annotation { "Feature Type Name" : "Feature", "Feature Type Description" : "" }
export const myFeature = defineFeature(function(context is Context, id is Id, definition is map)
    precondition{}
    {
        {
            var Q0;
            Q0=qCreatedBy(makeId("Front.planeOp"),FACE);
            var sketch = newSketch(context, id + "F0", { "sketchPlane" : qUnion([Q0])});
            skLineSegment(sketch, "E0.bottom", {"start": v(-34.13, 36.26) * mm, "end": v(34.87, 36.26) * mm});
            skLineSegment(sketch, "E0.top", {"start": v(-34.13, -16.74) * mm, "end": v(34.87, -16.74) * mm});
            skLineSegment(sketch, "E0.left", {"start": v(-34.13, 36.26) * mm, "end": v(-34.13, -16.74) * mm});
            skLineSegment(sketch, "E0.right", {"start": v(34.87, 36.26) * mm, "end": v(34.87, -16.74) * mm});
            skLineSegment(sketch, "E1", {"start": v(34.87, 23.26) * mm, "end": v(-34.13, 23.26) * mm});
            skLineSegment(sketch, "E2", {"start": v(31.87, 36.26) * mm, "end": v(31.87, 23.26) * mm});
            skLineSegment(sketch, "E3", {"start": v(31.87, 23.26) * mm, "end": v(34.87, 20.26) * mm});
            skLineSegment(sketch, "E4", {"start": v(31.87, -16.74) * mm, "end": v(31.87, 23.26) * mm});
            skLineSegment(sketch, "E5", {"start": v(31.87, -14.74) * mm, "end": v(34.87, -12.7) * mm});
            skLineSegment(sketch, "E6", {"start": v(30.87, 36.26) * mm, "end": v(31.87, 35.26) * mm});
            skCircle(sketch, "E7", {"center": v(-18.63, -14.24) * mm, "radius": 1.5 * mm});
            skCircle(sketch, "E8", {"center": v(-19.13, 33.76) * mm, "radius": 1.5 * mm});
            skCircle(sketch, "E9", {"center": v(32.37, 18.26) * mm, "radius": 1.5 * mm});
            skCircle(sketch, "E10", {"center": v(32.37, -9.74) * mm, "radius": 1.5 * mm});
            skSolve(sketch);
        }
        {
            var Q0;
            {var subQ1=sQuery(id+"F0.wireOp",EDGE,"E0.top");var subQ5=sQuery(id+"F0.wireOp",EDGE,"E0.left");var subQ8=makeQuery(id+"F0.imprint","INTERSECT",VERTEX,{"derivedFrom":[subQ1,subQ5]});Q0=makeQuery(id+"F0.imprint","IMPRINT",FACE,{"disambiguationData":[TD([[makeQuery(id+"F0.imprint","IMPRINT",EDGE,{"disambiguationData":[TD([[subQ8,-1.0]])],"derivedFrom":subQ1}),1.0]])]});}
            var Q1;
            {var subQ0=sQuery(id+"F0.wireOp",EDGE,"E3");Q1=makeQuery(id+"F0.imprint","IMPRINT",FACE,{"disambiguationData":[TD([[makeQuery(id+"F0.imprint","IMPRINT",EDGE,{"derivedFrom":subQ0}),-1.0]])]});}
            var Q2;
            {var subQ3=sQuery(id+"F0.wireOp",EDGE,"E6");Q2=makeQuery(id+"F0.imprint","IMPRINT",FACE,{"disambiguationData":[TD([[makeQuery(id+"F0.imprint","IMPRINT",EDGE,{"derivedFrom":subQ3}),-1.0]])]});}
            extrude(context, id + "F1", {"entities" : qUnion([Q0, Q1, Q2]), "depth" : 1 * mm});
        }
        {
            var Q0;
            Q0=makeQuery(id+"F1.opExtrude","CAP_FACE",FACE,{"disambiguationData":[OSD([sQuery(id+"F0.wireOp",EDGE,"E0.bottom"),sQuery(id+"F0.wireOp",EDGE,"E0.top"),sQuery(id+"F0.wireOp",EDGE,"E0.left"),sQuery(id+"F0.wireOp",EDGE,"E0.right"),sQuery(id+"F0.wireOp",EDGE,"E2"),sQuery(id+"F0.wireOp",EDGE,"E3"),sQuery(id+"F0.wireOp",EDGE,"E4"),sQuery(id+"F0.wireOp",EDGE,"E5"),sQuery(id+"F0.wireOp",EDGE,"E6"),sQuery(id+"F0.wireOp",EDGE,"E7"),sQuery(id+"F0.wireOp",EDGE,"E8"),sQuery(id+"F0.wireOp",EDGE,"E9"),sQuery(id+"F0.wireOp",EDGE,"E10")])],"isStart":false});
            var sketch = newSketch(context, id + "F2", { "sketchPlane" : qUnion([Q0])});
            skLineSegment(sketch, "E11.bottom", {"start": v(30.87, 35.26) * mm, "end": v(9.87, 35.26) * mm});
            skLineSegment(sketch, "E11.top", {"start": v(30.87, 33.26) * mm, "end": v(9.87, 33.26) * mm});
            skLineSegment(sketch, "E11.left", {"start": v(30.87, 35.26) * mm, "end": v(30.87, 33.26) * mm});
            skLineSegment(sketch, "E11.right", {"start": v(9.87, 35.26) * mm, "end": v(9.87, 33.26) * mm});
            skLineSegment(sketch, "E12.bottom", {"start": v(8.87, 35.26) * mm, "end": v(-12.13, 35.26) * mm});
            skLineSegment(sketch, "E12.top", {"start": v(8.87, 33.26) * mm, "end": v(-12.13, 33.26) * mm});
            skLineSegment(sketch, "E12.left", {"start": v(8.87, 35.26) * mm, "end": v(8.87, 33.26) * mm});
            skLineSegment(sketch, "E12.right", {"start": v(-12.13, 35.26) * mm, "end": v(-12.13, 33.26) * mm});
            skLineSegment(sketch, "E13.bottom", {"start": v(30.87, -15.74) * mm, "end": v(15.87, -15.74) * mm});
            skLineSegment(sketch, "E13.top", {"start": v(30.87, -13.74) * mm, "end": v(15.87, -13.74) * mm});
            skLineSegment(sketch, "E13.left", {"start": v(30.87, -15.74) * mm, "end": v(30.87, -13.74) * mm});
            skLineSegment(sketch, "E13.right", {"start": v(15.87, -15.74) * mm, "end": v(15.87, -13.74) * mm});
            skLineSegment(sketch, "E14.bottom", {"start": v(13.87, -15.74) * mm, "end": v(-1.13, -15.74) * mm});
            skLineSegment(sketch, "E14.top", {"start": v(13.87, -13.74) * mm, "end": v(-1.13, -13.74) * mm});
            skLineSegment(sketch, "E14.left", {"start": v(13.87, -15.74) * mm, "end": v(13.87, -13.74) * mm});
            skLineSegment(sketch, "E14.right", {"start": v(-1.13, -15.74) * mm, "end": v(-1.13, -13.74) * mm});
            skLineSegment(sketch, "E15.bottom", {"start": v(-19.65, 29.26) * mm, "end": v(-9.65, 29.26) * mm});
            skLineSegment(sketch, "E15.top", {"start": v(-19.65, 22.06) * mm, "end": v(-9.65, 22.06) * mm});
            skLineSegment(sketch, "E15.left", {"start": v(-19.65, 29.26) * mm, "end": v(-19.65, 22.06) * mm});
            skLineSegment(sketch, "E15.right", {"start": v(-9.65, 29.26) * mm, "end": v(-9.65, 22.06) * mm});
            skSolve(sketch);
        }
        {
            var Q0;
            Q0=makeQuery(id+"F1.opExtrude","CAP_FACE",FACE,{"disambiguationData":[OSD([sQuery(id+"F0.wireOp",EDGE,"E0.bottom"),sQuery(id+"F0.wireOp",EDGE,"E0.top"),sQuery(id+"F0.wireOp",EDGE,"E0.left"),sQuery(id+"F0.wireOp",EDGE,"E0.right"),sQuery(id+"F0.wireOp",EDGE,"E2"),sQuery(id+"F0.wireOp",EDGE,"E3"),sQuery(id+"F0.wireOp",EDGE,"E4"),sQuery(id+"F0.wireOp",EDGE,"E5"),sQuery(id+"F0.wireOp",EDGE,"E6"),sQuery(id+"F0.wireOp",EDGE,"E7"),sQuery(id+"F0.wireOp",EDGE,"E8"),sQuery(id+"F0.wireOp",EDGE,"E9"),sQuery(id+"F0.wireOp",EDGE,"E10")])],"isStart":false});
            var sketch = newSketch(context, id + "F3", { "sketchPlane" : qUnion([Q0])});
            skLineSegment(sketch, "E16.bottom", {"start": v(30.87, -5.74) * mm, "end": v(-5.13, -5.74) * mm});
            skLineSegment(sketch, "E16.top", {"start": v(30.87, 3.26) * mm, "end": v(-5.13, 3.26) * mm});
            skLineSegment(sketch, "E16.left", {"start": v(30.87, -5.74) * mm, "end": v(30.87, 3.26) * mm});
            skLineSegment(sketch, "E16.right", {"start": v(-5.13, -5.74) * mm, "end": v(-5.13, 3.26) * mm});
            skSolve(sketch);
        }
        {
            var Q0;
            Q0=qSketchRegion(id+"F3",true);
            extrude(context, id + "F4", {"entities" : qUnion([Q0]), "depth" : 8 * mm});
        }
        {
            var Q0;
            Q0=makeQuery(id+"F1.opExtrude","CAP_FACE",FACE,{"disambiguationData":[OSD([sQuery(id+"F0.wireOp",EDGE,"E0.bottom"),sQuery(id+"F0.wireOp",EDGE,"E0.top"),sQuery(id+"F0.wireOp",EDGE,"E0.left"),sQuery(id+"F0.wireOp",EDGE,"E0.right"),sQuery(id+"F0.wireOp",EDGE,"E2"),sQuery(id+"F0.wireOp",EDGE,"E3"),sQuery(id+"F0.wireOp",EDGE,"E4"),sQuery(id+"F0.wireOp",EDGE,"E5"),sQuery(id+"F0.wireOp",EDGE,"E6"),sQuery(id+"F0.wireOp",EDGE,"E7"),sQuery(id+"F0.wireOp",EDGE,"E8"),sQuery(id+"F0.wireOp",EDGE,"E9"),sQuery(id+"F0.wireOp",EDGE,"E10")])],"isStart":false});
            var sketch = newSketch(context, id + "F5", { "sketchPlane" : qUnion([Q0])});
            skLineSegment(sketch, "E17.bottom", {"start": v(23.87, 6.26) * mm, "end": v(18.87, 6.26) * mm});
            skLineSegment(sketch, "E17.top", {"start": v(23.87, 11.26) * mm, "end": v(18.87, 11.26) * mm});
            skLineSegment(sketch, "E17.left", {"start": v(23.87, 6.26) * mm, "end": v(23.87, 11.26) * mm});
            skLineSegment(sketch, "E17.right", {"start": v(18.87, 6.26) * mm, "end": v(18.87, 11.26) * mm});
            skCircle(sketch, "E18", {"center": v(21.37, 8.76) * mm, "radius": 1.5 * mm});
            skPoint(sketch, "E18.centerSnap0", {"position": v(23.87, 8.76) * mm});
            skSolve(sketch);
        }
        {
            var Q0;
            Q0=qSketchRegion(id+"F5",true);
            extrude(context, id + "F6", {"entities" : qUnion([Q0]), "depth" : 4 * mm});
        }
        {
            var Q0;
            Q0=makeQuery(id+"F1.opExtrude","CAP_FACE",FACE,{"disambiguationData":[OSD([sQuery(id+"F0.wireOp",EDGE,"E0.bottom"),sQuery(id+"F0.wireOp",EDGE,"E0.top"),sQuery(id+"F0.wireOp",EDGE,"E0.left"),sQuery(id+"F0.wireOp",EDGE,"E0.right"),sQuery(id+"F0.wireOp",EDGE,"E2"),sQuery(id+"F0.wireOp",EDGE,"E3"),sQuery(id+"F0.wireOp",EDGE,"E4"),sQuery(id+"F0.wireOp",EDGE,"E5"),sQuery(id+"F0.wireOp",EDGE,"E6"),sQuery(id+"F0.wireOp",EDGE,"E7"),sQuery(id+"F0.wireOp",EDGE,"E8"),sQuery(id+"F0.wireOp",EDGE,"E9"),sQuery(id+"F0.wireOp",EDGE,"E10")])],"isStart":false});
            var sketch = newSketch(context, id + "F7", { "sketchPlane" : qUnion([Q0])});
            skLineSegment(sketch, "E19.bottom", {"start": v(-23.13, -13.74) * mm, "end": v(-37.13, -13.74) * mm});
            skLineSegment(sketch, "E19.top", {"start": v(-23.13, -5.74) * mm, "end": v(-37.13, -5.74) * mm});
            skLineSegment(sketch, "E19.left", {"start": v(-23.13, -13.74) * mm, "end": v(-23.13, -5.74) * mm});
            skLineSegment(sketch, "E19.right", {"start": v(-37.13, -13.74) * mm, "end": v(-37.13, -5.74) * mm});
            skSolve(sketch);
        }
        {
            var Q0;
            Q0=qSketchRegion(id+"F7",true);
            extrude(context, id + "F8", {"entities" : qUnion([Q0]), "depth" : 10 * mm});
        }
        {
            var Q0;
            Q0=makeQuery(id+"F1.opExtrude","CAP_FACE",FACE,{"disambiguationData":[OSD([sQuery(id+"F0.wireOp",EDGE,"E0.bottom"),sQuery(id+"F0.wireOp",EDGE,"E0.top"),sQuery(id+"F0.wireOp",EDGE,"E0.left"),sQuery(id+"F0.wireOp",EDGE,"E0.right"),sQuery(id+"F0.wireOp",EDGE,"E2"),sQuery(id+"F0.wireOp",EDGE,"E3"),sQuery(id+"F0.wireOp",EDGE,"E4"),sQuery(id+"F0.wireOp",EDGE,"E5"),sQuery(id+"F0.wireOp",EDGE,"E6"),sQuery(id+"F0.wireOp",EDGE,"E7"),sQuery(id+"F0.wireOp",EDGE,"E8"),sQuery(id+"F0.wireOp",EDGE,"E9"),sQuery(id+"F0.wireOp",EDGE,"E10")])],"isStart":false});
            var sketch = newSketch(context, id + "F9", { "sketchPlane" : qUnion([Q0])});
            skLineSegment(sketch, "E20.bottom", {"start": v(-28.13, 21.26) * mm, "end": v(-36.13, 21.26) * mm});
            skLineSegment(sketch, "E20.top", {"start": v(-28.13, 28.26) * mm, "end": v(-36.13, 28.26) * mm});
            skLineSegment(sketch, "E20.left", {"start": v(-28.13, 21.26) * mm, "end": v(-28.13, 28.26) * mm});
            skLineSegment(sketch, "E20.right", {"start": v(-36.13, 21.26) * mm, "end": v(-36.13, 28.26) * mm});
            skSolve(sketch);
        }
        {
            var Q0;
            Q0=qSketchRegion(id+"F9",true);
            extrude(context, id + "F10", {"entities" : qUnion([Q0]), "depth" : 4 * mm});
        }
        {
            var Q0;
            Q0=makeQuery(id+"F1.opExtrude","CAP_FACE",FACE,{"disambiguationData":[OSD([sQuery(id+"F0.wireOp",EDGE,"E0.bottom"),sQuery(id+"F0.wireOp",EDGE,"E0.top"),sQuery(id+"F0.wireOp",EDGE,"E0.left"),sQuery(id+"F0.wireOp",EDGE,"E0.right"),sQuery(id+"F0.wireOp",EDGE,"E2"),sQuery(id+"F0.wireOp",EDGE,"E3"),sQuery(id+"F0.wireOp",EDGE,"E4"),sQuery(id+"F0.wireOp",EDGE,"E5"),sQuery(id+"F0.wireOp",EDGE,"E6"),sQuery(id+"F0.wireOp",EDGE,"E7"),sQuery(id+"F0.wireOp",EDGE,"E8"),sQuery(id+"F0.wireOp",EDGE,"E9"),sQuery(id+"F0.wireOp",EDGE,"E10")])],"isStart":false});
            var sketch = newSketch(context, id + "F11", { "sketchPlane" : qUnion([Q0])});
            skLineSegment(sketch, "E21.bottom", {"start": v(-34.13, 16.26) * mm, "end": v(-30.13, 16.26) * mm});
            skLineSegment(sketch, "E21.top", {"start": v(-34.13, 5.26) * mm, "end": v(-30.13, 5.26) * mm});
            skLineSegment(sketch, "E21.left", {"start": v(-34.13, 16.26) * mm, "end": v(-34.13, 5.26) * mm});
            skLineSegment(sketch, "E21.right", {"start": v(-30.13, 16.26) * mm, "end": v(-30.13, 5.26) * mm});
            skSolve(sketch);
        }
        {
            var Q0;
            Q0=qSketchRegion(id+"F11",true);
            extrude(context, id + "F12", {"entities" : qUnion([Q0]), "depth" : 5 * mm});
        }
        {
            var Q0;
            Q0=makeQuery(id+"F1.opExtrude","CAP_FACE",FACE,{"disambiguationData":[OSD([sQuery(id+"F0.wireOp",EDGE,"E0.bottom"),sQuery(id+"F0.wireOp",EDGE,"E0.top"),sQuery(id+"F0.wireOp",EDGE,"E0.left"),sQuery(id+"F0.wireOp",EDGE,"E0.right"),sQuery(id+"F0.wireOp",EDGE,"E2"),sQuery(id+"F0.wireOp",EDGE,"E3"),sQuery(id+"F0.wireOp",EDGE,"E4"),sQuery(id+"F0.wireOp",EDGE,"E5"),sQuery(id+"F0.wireOp",EDGE,"E6"),sQuery(id+"F0.wireOp",EDGE,"E7"),sQuery(id+"F0.wireOp",EDGE,"E8"),sQuery(id+"F0.wireOp",EDGE,"E9"),sQuery(id+"F0.wireOp",EDGE,"E10")])],"isStart":true});
            var sketch = newSketch(context, id + "F13", { "sketchPlane" : qUnion([Q0])});
            skText(sketch, "E22", { "text": "Olivia Xia\nDebbie Dong", "fontName": "AllertaStencil-Regular.ttf"});
            const initialGuessF13  = {"E22": [-0.00697, 0.0177, 1, 0, 0.00325]};
            skSetInitialGuess(sketch, initialGuessF13);
            skSolve(sketch);
        }
        {
            var Q0;
            Q0=qSketchRegion(id+"F13",true);
            extrude(context, id + "F14", {"entities" : qUnion([Q0]), "operationType" : NewBodyOperationType.ADD, "depth" : .1 * mm});
        }
        {
            var Q0;
            Q0=makeQuery(id+"F5.imprint","IMPRINT",FACE,{"disambiguationData":[TD([[makeQuery(id+"F5.imprint","IMPRINT",EDGE,{"derivedFrom":sQuery(id+"F5.wireOp",EDGE,"E18")}),1.0]])]});
            extrude(context, id + "F15", {"entities" : qUnion([Q0]), "depth" : 5 * mm});
        }
        {
            var Q0;
            Q0=makeQuery(id+"F2.imprint","IMPRINT",FACE,{"disambiguationData":[TD([[makeQuery(id+"F2.imprint","IMPRINT",EDGE,{"derivedFrom":sQuery(id+"F2.wireOp",EDGE,"E15.bottom")}),-1.0]])]});
            extrude(context, id + "F16", {"entities" : qUnion([Q0]), "depth" : 1 * mm});
        }
        {
            var Q0;
            Q0=makeQuery(id+"F2.imprint","IMPRINT",FACE,{"disambiguationData":[TD([[makeQuery(id+"F2.imprint","IMPRINT",EDGE,{"derivedFrom":sQuery(id+"F2.wireOp",EDGE,"E12.bottom")}),1.0]])]});
            var Q1;
            Q1=makeQuery(id+"F2.imprint","IMPRINT",FACE,{"disambiguationData":[TD([[makeQuery(id+"F2.imprint","IMPRINT",EDGE,{"derivedFrom":sQuery(id+"F2.wireOp",EDGE,"E11.bottom")}),1.0]])]});
            var Q2;
            Q2=makeQuery(id+"F2.imprint","IMPRINT",FACE,{"disambiguationData":[TD([[makeQuery(id+"F2.imprint","IMPRINT",EDGE,{"derivedFrom":sQuery(id+"F2.wireOp",EDGE,"E14.bottom")}),-1.0]])]});
            var Q3;
            Q3=makeQuery(id+"F2.imprint","IMPRINT",FACE,{"disambiguationData":[TD([[makeQuery(id+"F2.imprint","IMPRINT",EDGE,{"derivedFrom":sQuery(id+"F2.wireOp",EDGE,"E13.bottom")}),-1.0]])]});
            extrude(context, id + "F17", {"entities" : qUnion([Q0, Q1, Q2, Q3]), "depth" : 8 * mm});
        }
        {
            var Q0;
            Q0=makeQuery(id+"F1.opExtrude","CAP_FACE",FACE,{"disambiguationData":[OSD([sQuery(id+"F0.wireOp",EDGE,"E0.bottom"),sQuery(id+"F0.wireOp",EDGE,"E0.top"),sQuery(id+"F0.wireOp",EDGE,"E0.left"),sQuery(id+"F0.wireOp",EDGE,"E0.right"),sQuery(id+"F0.wireOp",EDGE,"E2"),sQuery(id+"F0.wireOp",EDGE,"E3"),sQuery(id+"F0.wireOp",EDGE,"E4"),sQuery(id+"F0.wireOp",EDGE,"E5"),sQuery(id+"F0.wireOp",EDGE,"E6"),sQuery(id+"F0.wireOp",EDGE,"E7"),sQuery(id+"F0.wireOp",EDGE,"E8"),sQuery(id+"F0.wireOp",EDGE,"E9"),sQuery(id+"F0.wireOp",EDGE,"E10")])],"isStart":false});
            var sketch = newSketch(context, id + "F18", { "sketchPlane" : qUnion([Q0])});
            skLineSegment(sketch, "E23.bottom", {"start": v(-31.63, 2.76) * mm, "end": v(-27.23, 2.76) * mm});
            skLineSegment(sketch, "E23.top", {"start": v(-31.63, -3.24) * mm, "end": v(-27.23, -3.24) * mm});
            skLineSegment(sketch, "E23.left", {"start": v(-31.63, 2.76) * mm, "end": v(-31.63, -3.24) * mm});
            skLineSegment(sketch, "E23.right", {"start": v(-27.23, 2.76) * mm, "end": v(-27.23, -3.24) * mm});
            skLineSegment(sketch, "E24.bottom", {"start": v(-28.61, 13.3) * mm, "end": v(-26.61, 13.3) * mm});
            skLineSegment(sketch, "E24.top", {"start": v(-28.61, 8.3) * mm, "end": v(-26.61, 8.3) * mm});
            skLineSegment(sketch, "E24.left", {"start": v(-28.61, 13.3) * mm, "end": v(-28.61, 8.3) * mm});
            skLineSegment(sketch, "E24.right", {"start": v(-26.61, 13.3) * mm, "end": v(-26.61, 8.3) * mm});
            skSolve(sketch);
        }
        {
            var Q0;
            Q0=makeQuery(id+"F18.imprint","IMPRINT",FACE,{"disambiguationData":[TD([[makeQuery(id+"F18.imprint","IMPRINT",EDGE,{"derivedFrom":sQuery(id+"F18.wireOp",EDGE,"E23.bottom")}),-1.0]])]});
            extrude(context, id + "F19", {"entities" : qUnion([Q0]), "depth" : 2 * mm});
        }
        {
            var Q0;
            Q0=makeQuery(id+"F18.imprint","IMPRINT",FACE,{"disambiguationData":[TD([[makeQuery(id+"F18.imprint","IMPRINT",EDGE,{"derivedFrom":sQuery(id+"F18.wireOp",EDGE,"E24.bottom")}),-1.0]])]});
            extrude(context, id + "F20", {"entities" : qUnion([Q0]), "depth" : 11 * mm});
        }
        {
            var Q0;
            Q0=makeQuery(id+"F1.opExtrude","CAP_FACE",FACE,{"disambiguationData":[OSD([sQuery(id+"F0.wireOp",EDGE,"E0.bottom"),sQuery(id+"F0.wireOp",EDGE,"E0.top"),sQuery(id+"F0.wireOp",EDGE,"E0.left"),sQuery(id+"F0.wireOp",EDGE,"E0.right"),sQuery(id+"F0.wireOp",EDGE,"E2"),sQuery(id+"F0.wireOp",EDGE,"E3"),sQuery(id+"F0.wireOp",EDGE,"E4"),sQuery(id+"F0.wireOp",EDGE,"E5"),sQuery(id+"F0.wireOp",EDGE,"E6"),sQuery(id+"F0.wireOp",EDGE,"E7"),sQuery(id+"F0.wireOp",EDGE,"E8"),sQuery(id+"F0.wireOp",EDGE,"E9"),sQuery(id+"F0.wireOp",EDGE,"E10")])],"isStart":false});
            var sketch = newSketch(context, id + "F21", { "sketchPlane" : qUnion([Q0])});
            skCircle(sketch, "E25", {"center": v(-5.32, -11.74) * mm, "radius": 3 * mm});
            skCircle(sketch, "E26", {"center": v(-11.85, -11.74) * mm, "radius": 3 * mm});
            skLineSegment(sketch, "E27", {"start": v(-14.29, -13.48) * mm, "end": v(-9.4, -13.48) * mm});
            skLineSegment(sketch, "E28", {"start": v(-7.88, -13.3) * mm, "end": v(-2.75, -13.3) * mm});
            skSolve(sketch);
        }
        {
            var Q0;
            {var subQ0=sQuery(id+"F21.wireOp",EDGE,"E27");Q0=makeQuery(id+"F21.imprint","IMPRINT",FACE,{"disambiguationData":[TD([[makeQuery(id+"F21.imprint","IMPRINT",EDGE,{"derivedFrom":subQ0}),1.0]])]});}
            var Q1;
            {var subQ0=sQuery(id+"F21.wireOp",EDGE,"E28");Q1=makeQuery(id+"F21.imprint","IMPRINT",FACE,{"disambiguationData":[TD([[makeQuery(id+"F21.imprint","IMPRINT",EDGE,{"derivedFrom":subQ0}),1.0]])]});}
            extrude(context, id + "F22", {"entities" : qUnion([Q0, Q1]), "depth" : 7 * mm});
        }
        {
            var Q0;
            {var subQ0=sQuery(id+"F21.wireOp",EDGE,"E27");Q0=makeQuery(id+"F21.imprint","IMPRINT",FACE,{"disambiguationData":[TD([[makeQuery(id+"F21.imprint","IMPRINT",EDGE,{"derivedFrom":subQ0}),-1.0]])]});}
            var Q1;
            {var subQ0=sQuery(id+"F21.wireOp",EDGE,"E28");Q1=makeQuery(id+"F21.imprint","IMPRINT",FACE,{"disambiguationData":[TD([[makeQuery(id+"F21.imprint","IMPRINT",EDGE,{"derivedFrom":subQ0}),-1.0]])]});}
            extrude(context, id + "F23", {"entities" : qUnion([Q0, Q1]), "depth" : 7 * mm});
        }
        {
            var Q0;
            Q0=makeQuery(id+"F1.opExtrude","CAP_FACE",FACE,{"disambiguationData":[OSD([sQuery(id+"F0.wireOp",EDGE,"E0.bottom"),sQuery(id+"F0.wireOp",EDGE,"E0.top"),sQuery(id+"F0.wireOp",EDGE,"E0.left"),sQuery(id+"F0.wireOp",EDGE,"E0.right"),sQuery(id+"F0.wireOp",EDGE,"E2"),sQuery(id+"F0.wireOp",EDGE,"E3"),sQuery(id+"F0.wireOp",EDGE,"E4"),sQuery(id+"F0.wireOp",EDGE,"E5"),sQuery(id+"F0.wireOp",EDGE,"E6"),sQuery(id+"F0.wireOp",EDGE,"E7"),sQuery(id+"F0.wireOp",EDGE,"E8"),sQuery(id+"F0.wireOp",EDGE,"E9"),sQuery(id+"F0.wireOp",EDGE,"E10")])],"isStart":false});
            var sketch = newSketch(context, id + "F24", { "sketchPlane" : qUnion([Q0])});
            skLineSegment(sketch, "E29.bottom", {"start": v(7.87, 12.26) * mm, "end": v(10.87, 12.26) * mm});
            skLineSegment(sketch, "E29.top", {"start": v(7.87, 7.26) * mm, "end": v(10.87, 7.26) * mm});
            skLineSegment(sketch, "E29.left", {"start": v(7.87, 12.26) * mm, "end": v(7.87, 7.26) * mm});
            skLineSegment(sketch, "E29.right", {"start": v(10.87, 12.26) * mm, "end": v(10.87, 7.26) * mm});
            skText(sketch, "E30", { "text": "OX, 7 & DD, 7", "fontName": "AllertaStencil-Regular.ttf"});
            const initialGuessF24  = {"E30": [0.00148, 0.02523, 1, 0, 0.00204]};
            skSetInitialGuess(sketch, initialGuessF24);
            skSolve(sketch);
        }
        {
            var Q0;
            Q0=qSketchRegion(id+"F24",true);
            extrude(context, id + "F25", {"entities" : qUnion([Q0]), "depth" : 1 * mm});
        }
    });